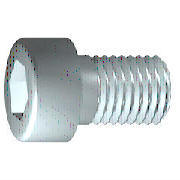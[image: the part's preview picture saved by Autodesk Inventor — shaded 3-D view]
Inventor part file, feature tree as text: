
AUTODESK INVENTOR PART (.ipt)
format: ipt  version: 2022 (Build 260153000, 153)  size: 193,024 bytes
history: native  units: mm (DEFAULTED — no unit token found)
features: sketch x2, other x1, extrude x1, plane x1, fillet x1
ambient origin geometry x7: Origin, YZ Plane, XY Plane, X Axis, Y Axis, Z Axis, Center Point
bodies: Solid1 (feature_tree)
feature tree (6):
  other  "Cuerpo"
  extrude  "Ranura"  Depth=2.5mm
  plane  "Work Plane1"
  fillet  "Fillet2"  Radius=2.5mm
  sketch  "Boceto1"  dims[d1=8.875mm d2=0.276153mm d3=2.5mm]
  sketch  "Boceto2"  dims[d4=1.1mm d5=60.0deg d6=2.5mm d7=2.5mm d8=2.309401mm d9=4.5mm d10=90.0deg d11=10.0mm d12=0.0mm d13=8.875mm d14=0.0mm d15=0.276052mm d16=0.276053mm d17=0.25mm d19=0.0mm d26=10.0mm d27=45.0deg d28=0.0mm d29=0.0mm d30=0.1mm]
